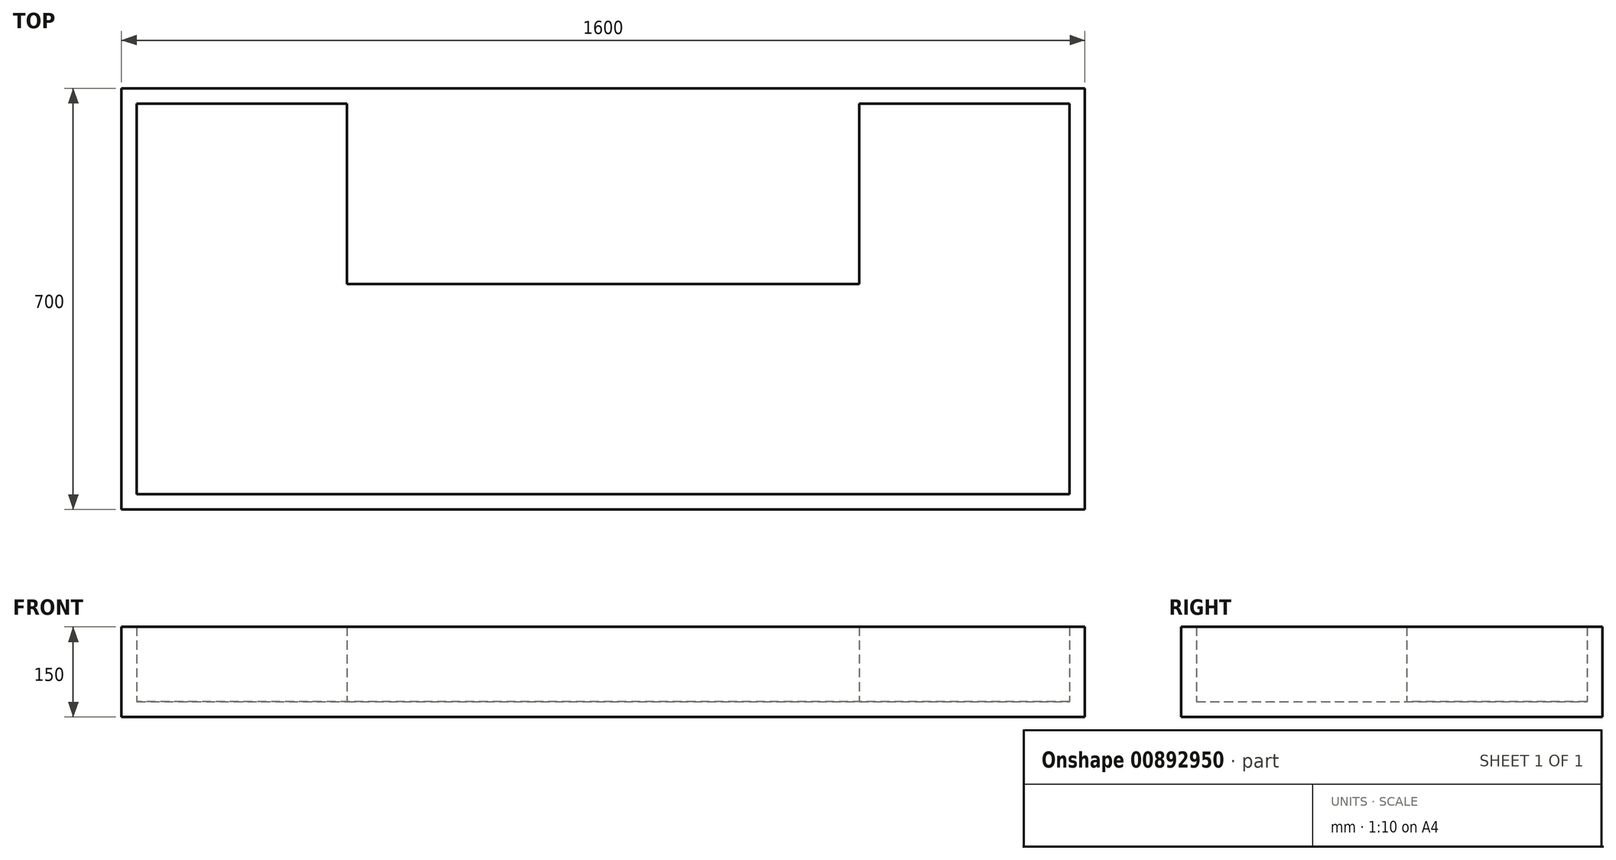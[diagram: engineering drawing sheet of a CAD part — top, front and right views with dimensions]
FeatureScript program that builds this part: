
annotation { "Feature Type Name" : "Feature", "Feature Type Description" : "" }
export const myFeature = defineFeature(function(context is Context, id is Id, definition is map)
    precondition{}
    {
        {
            var Q0;
            Q0=qCreatedBy(makeId("Top.planeOp"),FACE);
            var sketch = newSketch(context, id + "F0", { "sketchPlane" : qUnion([Q0])});
            skLineSegment(sketch, "E0", {"start": v(0, 0) * mm, "end": v(0, 700) * mm});
            skLineSegment(sketch, "E1", {"start": v(0, 700) * mm, "end": v(1600, 700) * mm});
            skLineSegment(sketch, "E2", {"start": v(1600, 700) * mm, "end": v(1600, 0) * mm});
            skLineSegment(sketch, "E3", {"start": v(1600, 0) * mm, "end": v(0, 0) * mm});
            skLineSegment(sketch, "E4", {"start": v(400, 700) * mm, "end": v(400, 400) * mm});
            skLineSegment(sketch, "E5", {"start": v(1200, 700) * mm, "end": v(1200, 400) * mm});
            skLineSegment(sketch, "E6", {"start": v(400, 400) * mm, "end": v(1200, 400) * mm});
            skSolve(sketch);
        }
        {
            var Q0;
            {var subQ3=sQuery(id+"F0.wireOp",EDGE,"E0");Q0=makeQuery(id+"F0.imprint","IMPRINT",FACE,{"disambiguationData":[TD([[makeQuery(id+"F0.imprint","IMPRINT",EDGE,{"derivedFrom":subQ3}),-1.0]])]});}
            extrude(context, id + "F1", {"entities" : qUnion([Q0]), "depth" : 150 * mm, "offsetDistance" : 25.4 * mm});
        }
        {
            var Q0;
            Q0=qCreatedBy(makeId("Top.planeOp"),FACE);
            var sketch = newSketch(context, id + "F2", { "sketchPlane" : qUnion([Q0])});
            skLineSegment(sketch, "E7", {"start": v(0, 0) * mm, "end": v(0, 700) * mm});
            skLineSegment(sketch, "E8", {"start": v(0, 700) * mm, "end": v(400, 700) * mm});
            skLineSegment(sketch, "E9", {"start": v(400, 700) * mm, "end": v(1200, 700) * mm});
            skLineSegment(sketch, "E10", {"start": v(400, 700) * mm, "end": v(400, 400) * mm});
            skLineSegment(sketch, "E11", {"start": v(1200, 700) * mm, "end": v(1200, 400) * mm});
            skLineSegment(sketch, "E12", {"start": v(1200, 700) * mm, "end": v(1600, 700) * mm});
            skLineSegment(sketch, "E13", {"start": v(400, 400) * mm, "end": v(1200, 400) * mm});
            skSolve(sketch);
        }
        {
            var Q0;
            Q0=makeQuery(id+"F1.opExtrude","CAP_FACE",FACE,{"disambiguationData":[OSD([sQuery(id+"F0.wireOp",EDGE,"E0"),sQuery(id+"F0.wireOp",EDGE,"E1"),sQuery(id+"F0.wireOp",EDGE,"E2"),sQuery(id+"F0.wireOp",EDGE,"E3"),sQuery(id+"F0.wireOp",EDGE,"E4"),sQuery(id+"F0.wireOp",EDGE,"E5"),sQuery(id+"F0.wireOp",EDGE,"E6")])],"isStart":false});
            shell(context, id + "F3", {"entities" : qUnion([Q0]), "thickness" : 25.4 * mm});
        }
        {
            var Q0;
            Q0=makeQuery(id+"F2.imprint","IMPRINT",FACE,{"disambiguationData":[TD([[makeQuery(id+"F2.imprint","IMPRINT",EDGE,{"derivedFrom":sQuery(id+"F2.wireOp",EDGE,"E9")}),-1.0]])]});
            extrude(context, id + "F4", {"entities" : qUnion([Q0]), "operationType" : NewBodyOperationType.ADD, "depth" : 150 * mm, "offsetDistance" : 25.4 * mm});
        }
    });
